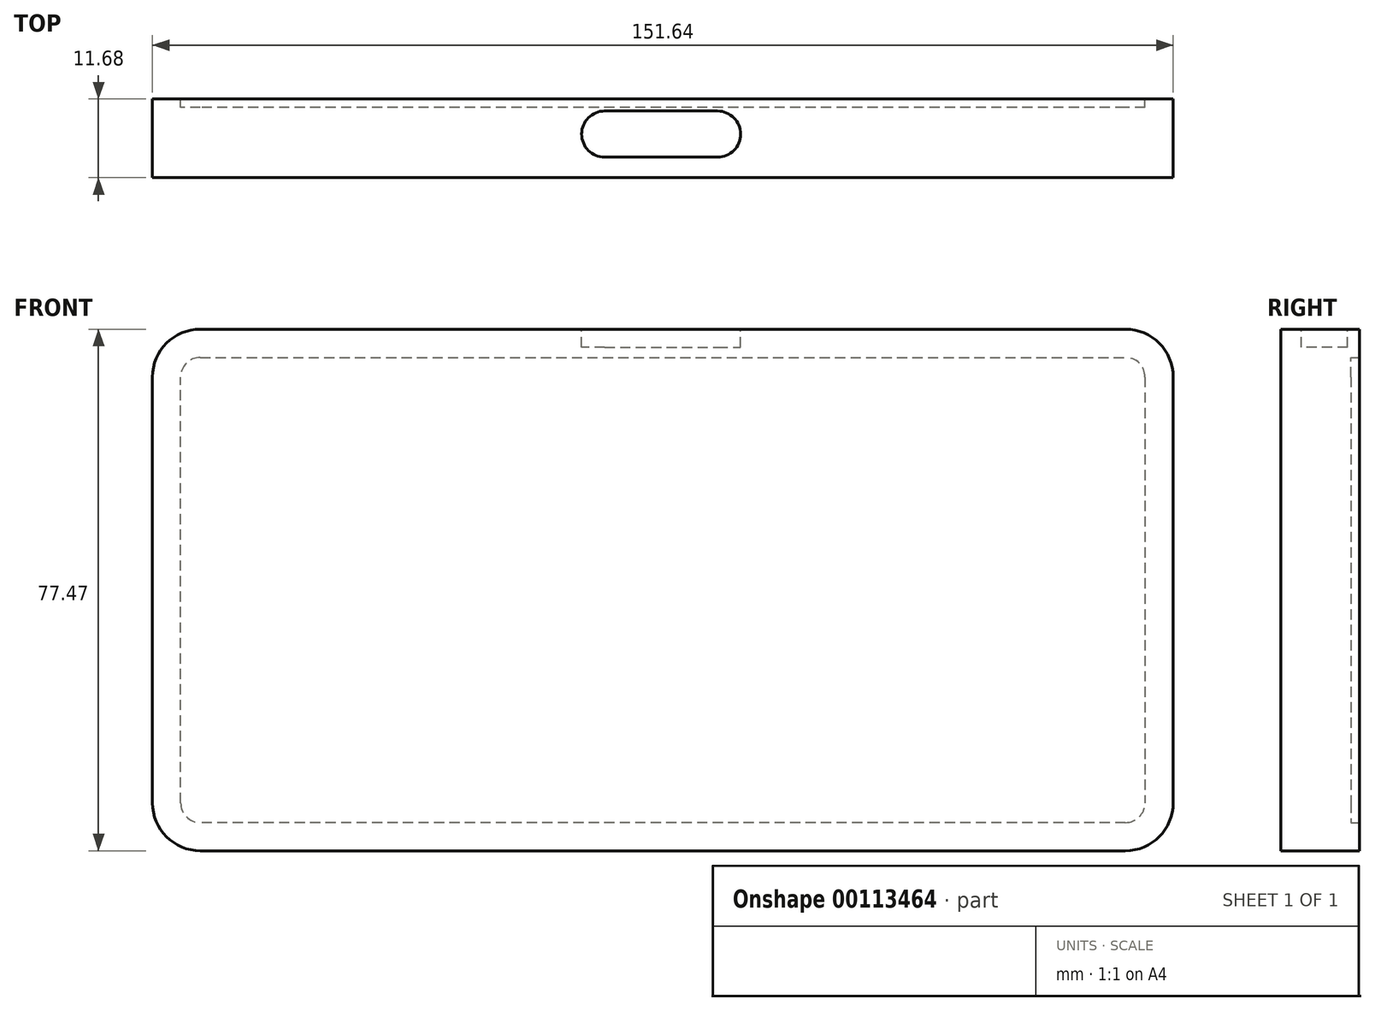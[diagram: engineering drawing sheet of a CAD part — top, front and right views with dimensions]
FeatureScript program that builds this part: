
annotation { "Feature Type Name" : "Feature", "Feature Type Description" : "" }
export const myFeature = defineFeature(function(context is Context, id is Id, definition is map)
    precondition{}
    {
        {
            var Q0;
            Q0=qCreatedBy(makeId("Front.planeOp"),FACE);
            var sketch = newSketch(context, id + "F0", { "sketchPlane" : qUnion([Q0])});
            skLineSegment(sketch, "E0.bottom", {"start": v(0, 0) * mm, "end": v(151.64, 0) * mm});
            skLineSegment(sketch, "E0.top", {"start": v(0, 77.47) * mm, "end": v(151.64, 77.47) * mm});
            skLineSegment(sketch, "E0.left", {"start": v(0, 0) * mm, "end": v(0, 77.47) * mm});
            skLineSegment(sketch, "E0.right", {"start": v(151.64, 0) * mm, "end": v(151.64, 77.47) * mm});
            skSolve(sketch);
        }
        {
            var Q0;
            Q0 = qSketchRegion(id + "F0", true);
            extrude(context, id + "F1", {"entities" : qUnion([Q0]), "depth" : 11.68 * mm});
        }
        {
            var Q0;
            Q0=makeQuery(id+"F1.opExtrude","SWEPT_EDGE",EDGE,{"disambiguationData":[OSD([sQuery(id+"F0.wireOp",EDGE,"E0.top"),sQuery(id+"F0.wireOp",EDGE,"E0.left")])]});
            var Q1;
            Q1=makeQuery(id+"F1.opExtrude","SWEPT_EDGE",EDGE,{"disambiguationData":[OSD([sQuery(id+"F0.wireOp",EDGE,"E0.top"),sQuery(id+"F0.wireOp",EDGE,"E0.right")])]});
            var Q2;
            Q2=makeQuery(id+"F1.opExtrude","SWEPT_EDGE",EDGE,{"disambiguationData":[OSD([sQuery(id+"F0.wireOp",EDGE,"E0.bottom"),sQuery(id+"F0.wireOp",EDGE,"E0.right")])]});
            var Q3;
            Q3=makeQuery(id+"F1.opExtrude","SWEPT_EDGE",EDGE,{"disambiguationData":[OSD([sQuery(id+"F0.wireOp",EDGE,"E0.bottom"),sQuery(id+"F0.wireOp",EDGE,"E0.left")])]});
            fillet(context, id + "F2", {"entities" : qUnion([Q0, Q1, Q2, Q3]), "radius" : 7.11 * mm, "tangentPropagation" : true, "allowEdgeOverflow" : false});
        }
        {
            var Q0;
            Q0=makeQuery(id+"F1.opExtrude","SWEPT_FACE",FACE,{"disambiguationData":[OSD([sQuery(id+"F0.wireOp",EDGE,"E0.top")])]});
            var sketch = newSketch(context, id + "F3", { "sketchPlane" : qUnion([Q0])});
            skLineSegment(sketch, "E1", {"start": v(67.18, -1.78) * mm, "end": v(83.95, -1.78) * mm});
            skArc(sketch, "E2", {"start": v(83.95, -8.64) * mm, "mid": v(87.38, -5.2) * mm, "end": v(83.95, -1.78) * mm});
            skArc(sketch, "E3", {"start": v(67.18, -1.78) * mm, "mid": v(63.75, -5.2) * mm, "end": v(67.18, -8.64) * mm});
            skLineSegment(sketch, "E4", {"start": v(67.18, -8.64) * mm, "end": v(83.95, -8.64) * mm});
            skSolve(sketch);
        }
        {
            var Q0;
            Q0 = qSketchRegion(id + "F3", true);
            extrude(context, id + "F4", {"entities" : qUnion([Q0]), "operationType" : NewBodyOperationType.REMOVE, "oppositeDirection" : true, "depth" : 2.67 * mm});
        }
        {
            var Q0;
            Q0=makeQuery(id+"F1.opExtrude","CAP_FACE",FACE,{"disambiguationData":[OSD([sQuery(id+"F0.wireOp",EDGE,"E0.bottom"),sQuery(id+"F0.wireOp",EDGE,"E0.top"),sQuery(id+"F0.wireOp",EDGE,"E0.left"),sQuery(id+"F0.wireOp",EDGE,"E0.right")])],"isStart":true});
            var sketch = newSketch(context, id + "F5", { "sketchPlane" : qUnion([Q0])});
            skArc(sketch, "E5.0", {"start": v(-147.45, 7.11) * mm, "mid": v(-146.6, 5.05) * mm, "end": v(-144.53, 4.2) * mm});
            skLineSegment(sketch, "E5.1", {"start": v(-147.45, 70.36) * mm, "end": v(-147.45, 7.11) * mm});
            skLineSegment(sketch, "E5.2", {"start": v(-144.53, 4.2) * mm, "end": v(-7.11, 4.2) * mm});
            skArc(sketch, "E5.3", {"start": v(-144.53, 73.28) * mm, "mid": v(-146.6, 72.42) * mm, "end": v(-147.45, 70.36) * mm});
            skArc(sketch, "E5.4", {"start": v(-7.11, 4.2) * mm, "mid": v(-5.05, 5.05) * mm, "end": v(-4.2, 7.11) * mm});
            skLineSegment(sketch, "E5.5", {"start": v(-4.2, 7.11) * mm, "end": v(-4.2, 70.36) * mm});
            skArc(sketch, "E5.6", {"start": v(-4.2, 70.36) * mm, "mid": v(-5.05, 72.42) * mm, "end": v(-7.11, 73.28) * mm});
            skLineSegment(sketch, "E5.7", {"start": v(-7.11, 73.28) * mm, "end": v(-144.53, 73.28) * mm});
            skSolve(sketch);
        }
        {
            var Q0;
            Q0 = qSketchRegion(id + "F5", true);
            extrude(context, id + "F6", {"entities" : qUnion([Q0]), "operationType" : NewBodyOperationType.REMOVE, "oppositeDirection" : true, "depth" : 1.27 * mm});
        }
    });
